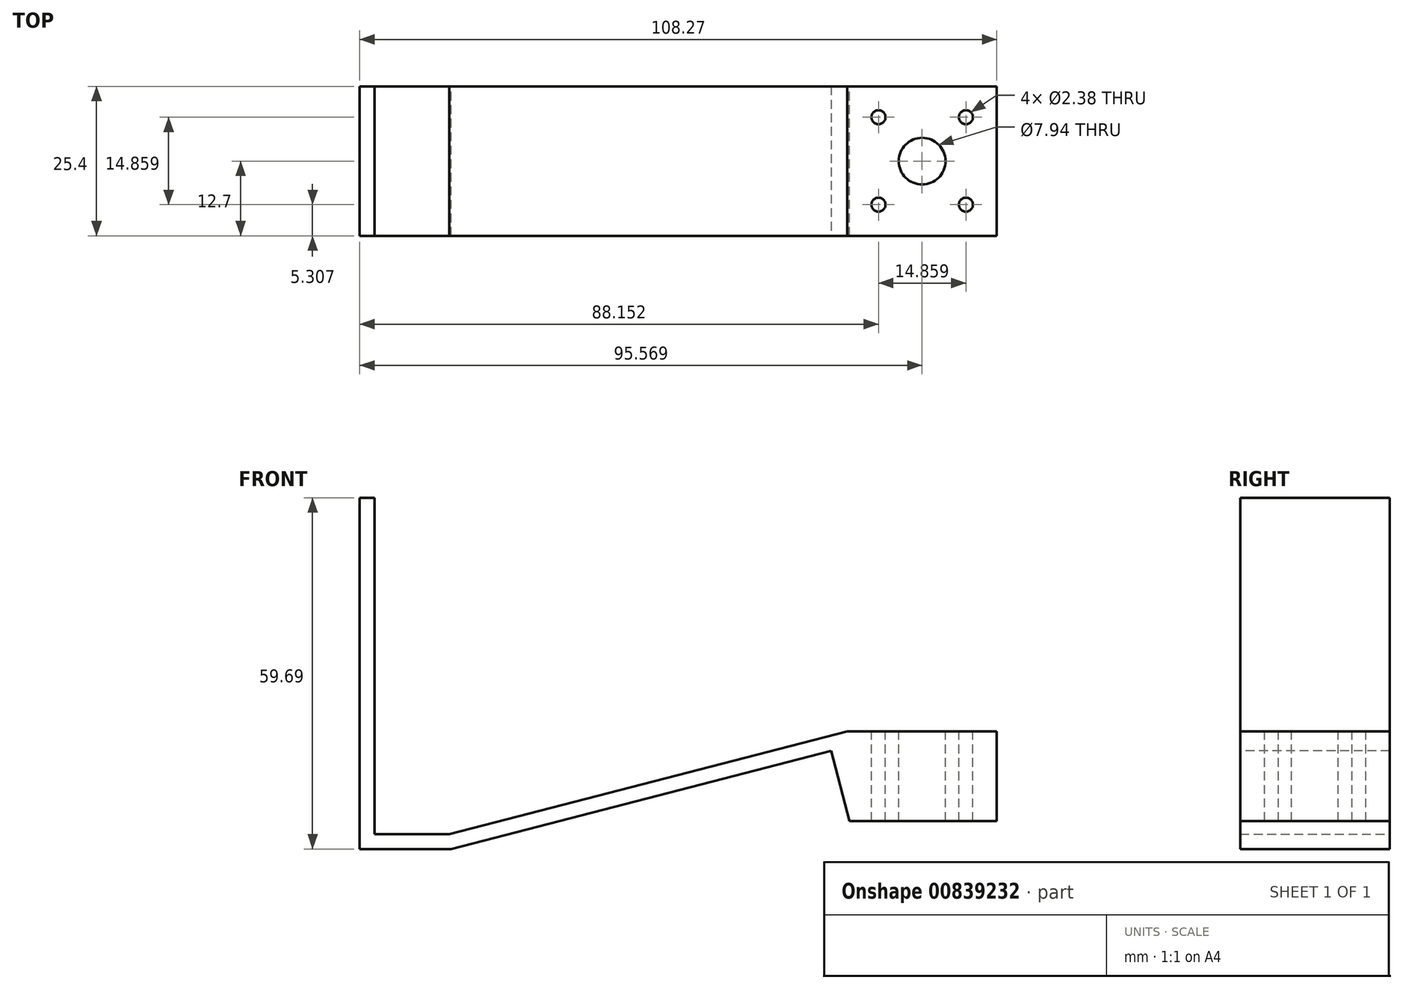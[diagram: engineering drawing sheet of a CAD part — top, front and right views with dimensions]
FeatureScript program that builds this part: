
annotation { "Feature Type Name" : "Feature", "Feature Type Description" : "" }
export const myFeature = defineFeature(function(context is Context, id is Id, definition is map)
    precondition{}
    {
        {
            var Q0;
            Q0=qCreatedBy(makeId("Front.planeOp"),FACE);
            var sketch = newSketch(context, id + "F0", { "sketchPlane" : qUnion([Q0])});
            skLineSegment(sketch, "E0", {"start": v(-50.26, 39.69) * mm, "end": v(-50.26, -17.46) * mm});
            skLineSegment(sketch, "E1", {"start": v(-50.26, -17.46) * mm, "end": v(-37.56, -17.46) * mm});
            skLineSegment(sketch, "E2", {"start": v(-37.56, -17.46) * mm, "end": v(30.07, 0) * mm});
            skLineSegment(sketch, "E3", {"start": v(30.07, 0) * mm, "end": v(55.47, 0) * mm});
            skLineSegment(sketch, "E4.0", {"start": v(30.4, -2.54) * mm, "end": v(55.47, -2.54) * mm});
            skLineSegment(sketch, "E4.1", {"start": v(-37.24, -20) * mm, "end": v(30.4, -2.54) * mm});
            skLineSegment(sketch, "E4.2", {"start": v(-52.8, -20) * mm, "end": v(-37.24, -20) * mm});
            skLineSegment(sketch, "E4.3", {"start": v(-52.8, 39.69) * mm, "end": v(-52.8, -20) * mm});
            skLineSegment(sketch, "E5", {"start": v(-52.8, 39.69) * mm, "end": v(-50.26, 39.69) * mm});
            skLineSegment(sketch, "E6", {"start": v(55.47, 0) * mm, "end": v(55.47, -2.54) * mm});
            skSolve(sketch);
        }
        {
            var Q0;
            Q0=makeQuery(id+"F0.imprint","IMPRINT",FACE,{"disambiguationData":[TD([[makeQuery(id+"F0.imprint","IMPRINT",EDGE,{"derivedFrom":sQuery(id+"F0.wireOp",EDGE,"E0")}),-1.0]])]});
            extrude(context, id + "F1", {"entities" : qUnion([Q0]), "depth" : 25.4 * mm, "offsetDistance" : 25.4 * mm});
        }
        {
            var Q0;
            Q0=makeQuery(id+"F1.opExtrude","SWEPT_FACE",FACE,{"disambiguationData":[OSD([sQuery(id+"F0.wireOp",EDGE,"E3")])]});
            var Q1;
            Q1=makeQuery(id+"F1.opExtrude","SWEPT_FACE",FACE,{"disambiguationData":[OSD([sQuery(id+"F0.wireOp",EDGE,"E3")])]});
            var sketch = newSketch(context, id + "F2", { "sketchPlane" : qUnion([Q0, Q1])});
            skCircle(sketch, "E7", {"center": v(42.77, -12.7) * mm, "radius": 3.97 * mm});
            skCircle(sketch, "E8", {"center": v(35.35, -5.23) * mm, "radius": 1.2 * mm});
            skCircle(sketch, "E9", {"center": v(50.21, -5.23) * mm, "radius": 1.2 * mm});
            skCircle(sketch, "E10", {"center": v(35.35, -20.1) * mm, "radius": 1.2 * mm});
            skCircle(sketch, "E11", {"center": v(50.21, -20.1) * mm, "radius": 1.2 * mm});
            skLineSegment(sketch, "E12", {"start": v(30.07, 0) * mm, "end": v(55.47, -25.4) * mm});
            skLineSegment(sketch, "E13", {"start": v(55.47, 0) * mm, "end": v(30.07, -25.4) * mm});
            skLineSegment(sketch, "E14.0", {"start": v(49.12, -6.35) * mm, "end": v(36.42, -6.35) * mm});
            skLineSegment(sketch, "E14.1", {"start": v(49.12, -19.05) * mm, "end": v(49.12, -6.35) * mm});
            skLineSegment(sketch, "E14.2", {"start": v(36.42, -19.05) * mm, "end": v(49.12, -19.05) * mm});
            skLineSegment(sketch, "E14.3", {"start": v(36.42, -6.35) * mm, "end": v(36.42, -19.05) * mm});
            skSolve(sketch);
        }
        {
            var Q0;
            Q0=makeQuery(id+"F1.opExtrude","SWEPT_FACE",FACE,{"disambiguationData":[OSD([sQuery(id+"F0.wireOp",EDGE,"E4.0")])]});
            extrude(context, id + "F3", {"entities" : qUnion([Q0]), "operationType" : NewBodyOperationType.ADD, "depth" : 12.7 * mm, "offsetDistance" : 25.4 * mm});
        }
        {
            var Q0;
            {var subQ0=sQuery(id+"F0.wireOp",EDGE,"E4.0");Q0=makeQuery(id+"F3.boolean.opBoolean","MERGE",FACE,{"derivedFrom":[makeQuery(id+"F1.opExtrude","CAP_FACE",FACE,{"disambiguationData":[OSD([sQuery(id+"F0.wireOp",EDGE,"E0"),sQuery(id+"F0.wireOp",EDGE,"E1"),sQuery(id+"F0.wireOp",EDGE,"E2"),sQuery(id+"F0.wireOp",EDGE,"E3"),subQ0,sQuery(id+"F0.wireOp",EDGE,"E4.1"),sQuery(id+"F0.wireOp",EDGE,"E4.2"),sQuery(id+"F0.wireOp",EDGE,"E4.3"),sQuery(id+"F0.wireOp",EDGE,"E5"),sQuery(id+"F0.wireOp",EDGE,"E6")])],"isStart":false}),makeQuery(id+"F3.opExtrude","SWEPT_FACE",FACE,{"disambiguationData":[OSD([subQ0]),TDD([makeQuery(id+"F1.opExtrude","CAP_EDGE",EDGE,{"disambiguationData":[OSD([subQ0])],"isStart":false})])]})]});}
            var sketch = newSketch(context, id + "F4", { "sketchPlane" : qUnion([Q0])});
            skLineSegment(sketch, "E15", {"start": v(30.4, -15.24) * mm, "end": v(27.32, -3.33) * mm});
            skSolve(sketch);
        }
        {
            var Q0;
            {var subQ0=sQuery(id+"F4.wireOp",EDGE,"E15");Q0=makeQuery(id+"F4.imprint","IMPRINT",FACE,{"disambiguationData":[TD([[makeQuery(id+"F4.imprint","IMPRINT",EDGE,{"derivedFrom":subQ0}),-1.0]])]});}
            extrude(context, id + "F5", {"entities" : qUnion([Q0]), "operationType" : NewBodyOperationType.ADD, "oppositeDirection" : true, "depth" : 25.4 * mm, "offsetDistance" : 25.4 * mm});
        }
        {
            var Q0;
            {var subQ0=sQuery(id+"F2.wireOp",EDGE,"E12");var subQ1=sQuery(id+"F2.wireOp",EDGE,"E7");var subQ2=makeQuery(id+"F2.imprint","INTERSECT",VERTEX,{"disambiguationData":[OD(0.0)],"derivedFrom":[subQ1,subQ0]});Q0=makeQuery(id+"F2.imprint","IMPRINT",FACE,{"disambiguationData":[TD([[makeQuery(id+"F2.imprint","IMPRINT",EDGE,{"disambiguationData":[TD([[subQ2,1.0]])],"derivedFrom":subQ1}),1.0]])]});}
            var Q1;
            {var subQ0=sQuery(id+"F2.wireOp",EDGE,"E13");var subQ1=sQuery(id+"F2.wireOp",EDGE,"E7");var subQ2=makeQuery(id+"F2.imprint","INTERSECT",VERTEX,{"disambiguationData":[OD(0.0)],"derivedFrom":[subQ1,subQ0]});Q1=makeQuery(id+"F2.imprint","IMPRINT",FACE,{"disambiguationData":[TD([[makeQuery(id+"F2.imprint","IMPRINT",EDGE,{"disambiguationData":[TD([[subQ2,1.0]])],"derivedFrom":subQ1}),1.0]])]});}
            var Q2;
            {var subQ0=sQuery(id+"F2.wireOp",EDGE,"E13");var subQ1=sQuery(id+"F2.wireOp",EDGE,"E7");var subQ2=makeQuery(id+"F2.imprint","INTERSECT",VERTEX,{"disambiguationData":[OD(1.0)],"derivedFrom":[subQ1,subQ0]});Q2=makeQuery(id+"F2.imprint","IMPRINT",FACE,{"disambiguationData":[TD([[makeQuery(id+"F2.imprint","IMPRINT",EDGE,{"disambiguationData":[TD([[subQ2,-1.0]])],"derivedFrom":subQ1}),1.0]])]});}
            var Q3;
            {var subQ0=sQuery(id+"F2.wireOp",EDGE,"E12");var subQ1=sQuery(id+"F2.wireOp",EDGE,"E7");var subQ2=makeQuery(id+"F2.imprint","INTERSECT",VERTEX,{"disambiguationData":[OD(0.0)],"derivedFrom":[subQ1,subQ0]});Q3=makeQuery(id+"F2.imprint","IMPRINT",FACE,{"disambiguationData":[TD([[makeQuery(id+"F2.imprint","IMPRINT",EDGE,{"disambiguationData":[TD([[subQ2,-1.0]])],"derivedFrom":subQ1}),1.0]])]});}
            var Q4;
            {var subQ0=sQuery(id+"F2.wireOp",EDGE,"E13");var subQ1=sQuery(id+"F2.wireOp",EDGE,"E9");var subQ2=makeQuery(id+"F2.imprint","INTERSECT",VERTEX,{"disambiguationData":[OD(0.0)],"derivedFrom":[subQ1,subQ0]});Q4=makeQuery(id+"F2.imprint","IMPRINT",FACE,{"disambiguationData":[TD([[makeQuery(id+"F2.imprint","IMPRINT",EDGE,{"disambiguationData":[TD([[subQ2,-1.0]])],"derivedFrom":subQ1}),1.0]])]});}
            var Q5;
            {var subQ0=sQuery(id+"F2.wireOp",EDGE,"E13");var subQ1=sQuery(id+"F2.wireOp",EDGE,"E9");var subQ2=makeQuery(id+"F2.imprint","INTERSECT",VERTEX,{"disambiguationData":[OD(0.0)],"derivedFrom":[subQ1,subQ0]});Q5=makeQuery(id+"F2.imprint","IMPRINT",FACE,{"disambiguationData":[TD([[makeQuery(id+"F2.imprint","IMPRINT",EDGE,{"disambiguationData":[TD([[subQ2,1.0]])],"derivedFrom":subQ1}),1.0]])]});}
            var Q6;
            {var subQ0=sQuery(id+"F2.wireOp",EDGE,"E12");var subQ1=sQuery(id+"F2.wireOp",EDGE,"E11");var subQ2=makeQuery(id+"F2.imprint","INTERSECT",VERTEX,{"disambiguationData":[OD(0.0)],"derivedFrom":[subQ1,subQ0]});Q6=makeQuery(id+"F2.imprint","IMPRINT",FACE,{"disambiguationData":[TD([[makeQuery(id+"F2.imprint","IMPRINT",EDGE,{"disambiguationData":[TD([[subQ2,1.0]])],"derivedFrom":subQ1}),1.0]])]});}
            var Q7;
            {var subQ0=sQuery(id+"F2.wireOp",EDGE,"E12");var subQ1=sQuery(id+"F2.wireOp",EDGE,"E11");var subQ2=makeQuery(id+"F2.imprint","INTERSECT",VERTEX,{"disambiguationData":[OD(0.0)],"derivedFrom":[subQ1,subQ0]});Q7=makeQuery(id+"F2.imprint","IMPRINT",FACE,{"disambiguationData":[TD([[makeQuery(id+"F2.imprint","IMPRINT",EDGE,{"disambiguationData":[TD([[subQ2,-1.0]])],"derivedFrom":subQ1}),1.0]])]});}
            var Q8;
            {var subQ0=sQuery(id+"F2.wireOp",EDGE,"E13");var subQ1=sQuery(id+"F2.wireOp",EDGE,"E10");var subQ2=makeQuery(id+"F2.imprint","INTERSECT",VERTEX,{"disambiguationData":[OD(0.0)],"derivedFrom":[subQ1,subQ0]});Q8=makeQuery(id+"F2.imprint","IMPRINT",FACE,{"disambiguationData":[TD([[makeQuery(id+"F2.imprint","IMPRINT",EDGE,{"disambiguationData":[TD([[subQ2,1.0]])],"derivedFrom":subQ1}),1.0]])]});}
            var Q9;
            {var subQ0=sQuery(id+"F2.wireOp",EDGE,"E13");var subQ1=sQuery(id+"F2.wireOp",EDGE,"E10");var subQ2=makeQuery(id+"F2.imprint","INTERSECT",VERTEX,{"disambiguationData":[OD(0.0)],"derivedFrom":[subQ1,subQ0]});Q9=makeQuery(id+"F2.imprint","IMPRINT",FACE,{"disambiguationData":[TD([[makeQuery(id+"F2.imprint","IMPRINT",EDGE,{"disambiguationData":[TD([[subQ2,-1.0]])],"derivedFrom":subQ1}),1.0]])]});}
            var Q10;
            {var subQ0=sQuery(id+"F2.wireOp",EDGE,"E12");var subQ1=sQuery(id+"F2.wireOp",EDGE,"E8");var subQ2=makeQuery(id+"F2.imprint","INTERSECT",VERTEX,{"disambiguationData":[OD(0.0)],"derivedFrom":[subQ1,subQ0]});Q10=makeQuery(id+"F2.imprint","IMPRINT",FACE,{"disambiguationData":[TD([[makeQuery(id+"F2.imprint","IMPRINT",EDGE,{"disambiguationData":[TD([[subQ2,-1.0]])],"derivedFrom":subQ1}),1.0]])]});}
            var Q11;
            {var subQ0=sQuery(id+"F2.wireOp",EDGE,"E12");var subQ1=sQuery(id+"F2.wireOp",EDGE,"E8");var subQ2=makeQuery(id+"F2.imprint","INTERSECT",VERTEX,{"disambiguationData":[OD(0.0)],"derivedFrom":[subQ1,subQ0]});Q11=makeQuery(id+"F2.imprint","IMPRINT",FACE,{"disambiguationData":[TD([[makeQuery(id+"F2.imprint","IMPRINT",EDGE,{"disambiguationData":[TD([[subQ2,1.0]])],"derivedFrom":subQ1}),1.0]])]});}
            var Q12;
            Q12=sQuery(id+"F2.wireOp",EDGE,"E8");
            var Q13;
            Q13=sQuery(id+"F2.wireOp",EDGE,"E7");
            var Q14;
            Q14=sQuery(id+"F2.wireOp",EDGE,"E9");
            var Q15;
            Q15=sQuery(id+"F2.wireOp",EDGE,"E11");
            var Q16;
            Q16=sQuery(id+"F2.wireOp",EDGE,"E10");
            extrude(context, id + "F6", {"entities" : qUnion([Q0, Q1, Q2, Q3, Q4, Q5, Q6, Q7, Q8, Q9, Q10, Q11]), "operationType" : NewBodyOperationType.REMOVE, "surfaceEntities" : qUnion([Q12, Q13, Q14, Q15, Q16]), "endBound" : BoundingType.THROUGH_ALL, "oppositeDirection" : true, "depth" : 27.36 * mm, "offsetDistance" : 25.4 * mm});
        }
    });
